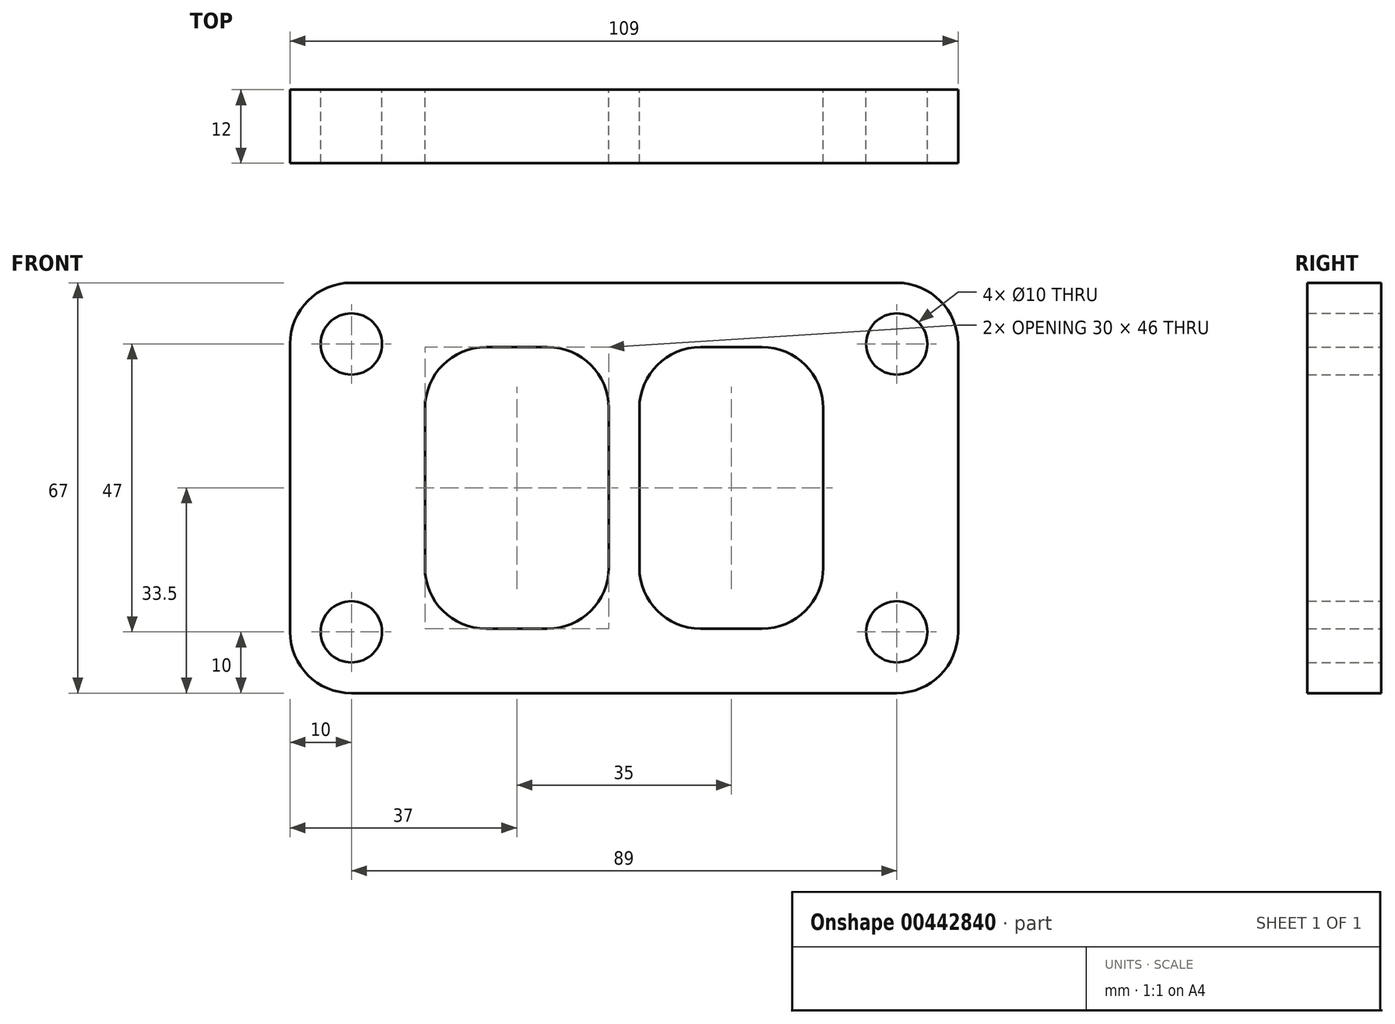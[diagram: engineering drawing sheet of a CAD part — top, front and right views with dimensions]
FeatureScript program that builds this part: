
annotation { "Feature Type Name" : "Feature", "Feature Type Description" : "" }
export const myFeature = defineFeature(function(context is Context, id is Id, definition is map)
    precondition{}
    {
        {
            var Q0;
            Q0=qCreatedBy(makeId("Front.planeOp"),FACE);
            var sketch = newSketch(context, id + "F0", { "sketchPlane" : qUnion([Q0])});
            skLineSegment(sketch, "E0.bottom", {"start": v(-44.5, 33.5) * mm, "end": v(44.5, 33.5) * mm});
            skLineSegment(sketch, "E0.top", {"start": v(-44.5, -33.5) * mm, "end": v(44.5, -33.5) * mm});
            skLineSegment(sketch, "E0.left", {"start": v(-54.5, 23.5) * mm, "end": v(-54.5, -23.5) * mm});
            skLineSegment(sketch, "E0.right", {"start": v(54.5, 23.5) * mm, "end": v(54.5, -23.5) * mm});
            skPoint(sketch, "E0.middle", {"position": v(0, 0) * mm});
            skPoint(sketch, "E1.visualSharp", {"position": v(-54.5, 33.5) * mm});
            skArc(sketch, "E1.filletArc", {"start": v(-44.5, 33.5) * mm, "mid": v(-51.57, 30.57) * mm, "end": v(-54.5, 23.5) * mm});
            skPoint(sketch, "E2.visualSharp", {"position": v(54.5, 33.5) * mm});
            skArc(sketch, "E2.filletArc", {"start": v(54.5, 23.5) * mm, "mid": v(51.57, 30.57) * mm, "end": v(44.5, 33.5) * mm});
            skPoint(sketch, "E3.visualSharp", {"position": v(54.5, -33.5) * mm});
            skArc(sketch, "E3.filletArc", {"start": v(44.5, -33.5) * mm, "mid": v(51.57, -30.57) * mm, "end": v(54.5, -23.5) * mm});
            skPoint(sketch, "E4.visualSharp", {"position": v(-54.5, -33.5) * mm});
            skArc(sketch, "E4.filletArc", {"start": v(-54.5, -23.5) * mm, "mid": v(-51.57, -30.57) * mm, "end": v(-44.5, -33.5) * mm});
            skCircle(sketch, "E5", {"center": v(-44.5, 23.5) * mm, "radius": 5 * mm});
            skCircle(sketch, "E6", {"center": v(44.5, 23.5) * mm, "radius": 5 * mm});
            skCircle(sketch, "E7", {"center": v(44.5, -23.5) * mm, "radius": 5 * mm});
            skCircle(sketch, "E8", {"center": v(-44.5, -23.5) * mm, "radius": 5 * mm});
            skLineSegment(sketch, "E9", {"start": v(0, 0) * mm, "end": v(-2.5, 0) * mm, "construction": true});
            skLineSegment(sketch, "E10", {"start": v(-2.5, 0) * mm, "end": v(-2.5, 13) * mm, "construction": true});
            skLineSegment(sketch, "E11", {"start": v(0, 0) * mm, "end": v(2.5, 0) * mm, "construction": true});
            skLineSegment(sketch, "E12", {"start": v(-2.5, 0) * mm, "end": v(-2.5, 23) * mm});
            skLineSegment(sketch, "E13", {"start": v(-12.5, 23) * mm, "end": v(-22.5, 23) * mm});
            skLineSegment(sketch, "E14", {"start": v(-32.5, 13) * mm, "end": v(-32.5, 0) * mm});
            skLineSegment(sketch, "E15", {"start": v(-32.5, 0) * mm, "end": v(-32.5, -13) * mm});
            skLineSegment(sketch, "E16", {"start": v(-22.5, -23) * mm, "end": v(-12.5, -23) * mm});
            skLineSegment(sketch, "E17", {"start": v(-2.5, -13) * mm, "end": v(-2.5, 0) * mm});
            skLineSegment(sketch, "E18", {"start": v(32.5, 13) * mm, "end": v(32.5, -13) * mm});
            skLineSegment(sketch, "E19", {"start": v(22.5, -23) * mm, "end": v(12.5, -23) * mm});
            skLineSegment(sketch, "E20", {"start": v(2.5, -13) * mm, "end": v(2.5, 0) * mm});
            skPoint(sketch, "E21.visualSharp", {"position": v(-32.5, 23) * mm});
            skArc(sketch, "E21.filletArc", {"start": v(-22.5, 23) * mm, "mid": v(-29.57, 20.07) * mm, "end": v(-32.5, 13) * mm});
            skPoint(sketch, "E22.newPointA", {"position": v(-2.5, 23) * mm});
            skArc(sketch, "E22.filletArc", {"start": v(-2.5, 13) * mm, "mid": v(-5.43, 20.07) * mm, "end": v(-12.5, 23) * mm});
            skPoint(sketch, "E23.visualSharp", {"position": v(-32.5, -23) * mm});
            skArc(sketch, "E23.filletArc", {"start": v(-32.5, -13) * mm, "mid": v(-29.57, -20.07) * mm, "end": v(-22.5, -23) * mm});
            skPoint(sketch, "E24.visualSharp", {"position": v(-2.5, -23) * mm});
            skArc(sketch, "E24.filletArc", {"start": v(-12.5, -23) * mm, "mid": v(-5.43, -20.07) * mm, "end": v(-2.5, -13) * mm});
            skPoint(sketch, "E25.visualSharp", {"position": v(32.5, 23) * mm});
            skArc(sketch, "E25.filletArc", {"start": v(32.5, 13) * mm, "mid": v(29.57, 20.07) * mm, "end": v(22.5, 23) * mm});
            skPoint(sketch, "E26.visualSharp", {"position": v(32.5, -23) * mm});
            skArc(sketch, "E26.filletArc", {"start": v(22.5, -23) * mm, "mid": v(29.57, -20.07) * mm, "end": v(32.5, -13) * mm});
            skPoint(sketch, "E27.visualSharp", {"position": v(2.5, -23) * mm});
            skArc(sketch, "E27.filletArc", {"start": v(2.5, -13) * mm, "mid": v(5.43, -20.07) * mm, "end": v(12.5, -23) * mm});
            skPoint(sketch, "E28.visualSharp", {"position": v(2.5, 23) * mm});
            skLineSegment(sketch, "E29", {"start": v(2.5, 0) * mm, "end": v(2.5, 13) * mm});
            skLineSegment(sketch, "E30", {"start": v(22.5, 23) * mm, "end": v(12.5, 23) * mm});
            skArc(sketch, "E31.filletArc", {"start": v(12.5, 23) * mm, "mid": v(5.43, 20.07) * mm, "end": v(2.5, 13) * mm});
            skLineSegment(sketch, "E32", {"start": v(-54.5, 0) * mm, "end": v(-32.5, 0) * mm, "construction": true});
            skLineSegment(sketch, "E33", {"start": v(32.5, 0) * mm, "end": v(54.5, 0) * mm, "construction": true});
            skLineSegment(sketch, "E34", {"start": v(-22.5, -23) * mm, "end": v(-22.5, -33.5) * mm, "construction": true});
            skLineSegment(sketch, "E35", {"start": v(22.5, -23) * mm, "end": v(22.5, -33.5) * mm, "construction": true});
            skLineSegment(sketch, "E36", {"start": v(-44.5, 23.5) * mm, "end": v(-44.5, -23.5) * mm, "construction": true});
            skLineSegment(sketch, "E37", {"start": v(-44.5, 23.5) * mm, "end": v(44.5, 23.5) * mm, "construction": true});
            skSolve(sketch);
        }
        {
            var Q0;
            Q0 = qSketchRegion(id + "F0", true);
            extrude(context, id + "F1", {"entities" : qUnion([Q0]), "depth" : 12 * mm, "offsetDistance" : 25 * mm});
        }
    });
